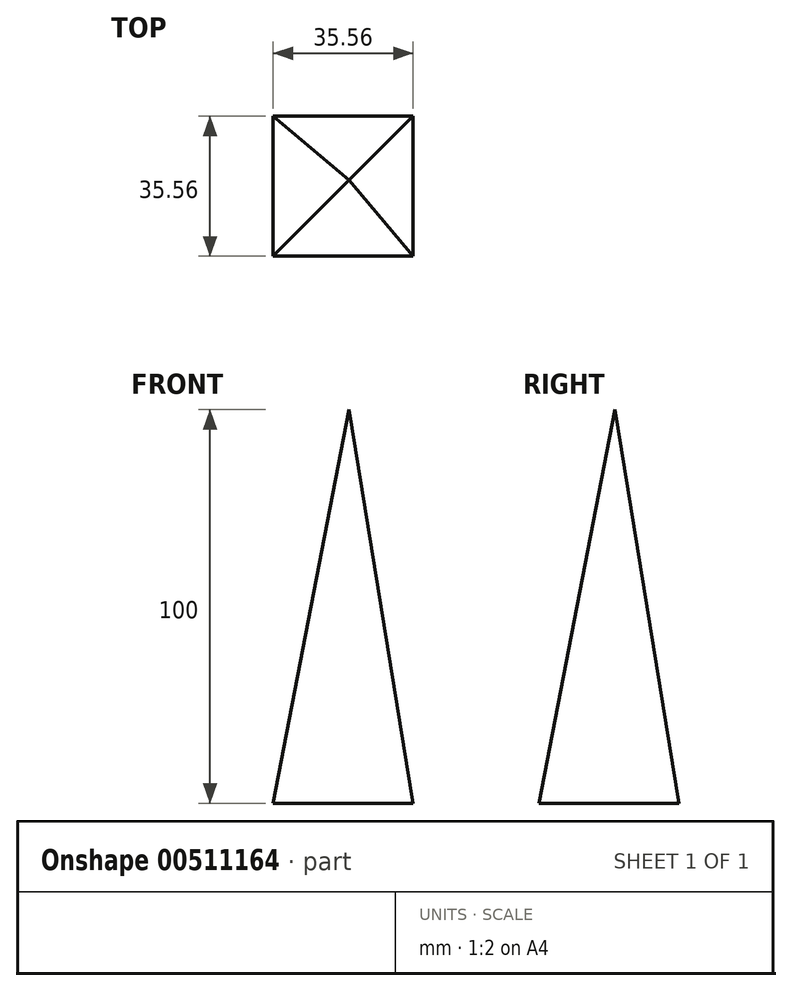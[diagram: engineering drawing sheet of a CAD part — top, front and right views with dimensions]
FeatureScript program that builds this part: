
annotation { "Feature Type Name" : "Feature", "Feature Type Description" : "" }
export const myFeature = defineFeature(function(context is Context, id is Id, definition is map)
    precondition{}
    {
        {
            var Q0;
            Q0=qCreatedBy(makeId("Top.planeOp"),FACE);
            var sketch = newSketch(context, id + "F0", { "sketchPlane" : qUnion([Q0])});
            skLineSegment(sketch, "E0", {"start": v(-19.24, 19.1) * mm, "end": v(-19.24, -16.47) * mm});
            skLineSegment(sketch, "E1", {"start": v(-19.24, -16.47) * mm, "end": v(16.32, -16.47) * mm});
            skLineSegment(sketch, "E2", {"start": v(16.32, -16.47) * mm, "end": v(16.32, 19.1) * mm});
            skLineSegment(sketch, "E3", {"start": v(17.2, 19.1) * mm, "end": v(-19.24, 19.1) * mm});
            skSolve(sketch);
        }
        {
            var Q0;
            Q0=qCreatedBy(makeId("Top.planeOp"),FACE);
            cPlane(context, id + "F1", {"entities" : qUnion([Q0]), "cplaneType" : CPlaneType.OFFSET, "offset" : 100 * mm, "width" : 152.4 * mm, "height" : 152.4 * mm});
        }
        {
            var Q0;
            Q0=qCreatedBy(id+"F1.planeOp",FACE);
            var sketch = newSketch(context, id + "F2", { "sketchPlane" : qUnion([Q0])});
            skPoint(sketch, "E4", {"position": v(0, 2.87) * mm});
            skSolve(sketch);
        }
        {
            var Q0;
            {var subQ0=sQuery(id+"F0.wireOp",EDGE,"E0");Q0=makeQuery(id+"F0.imprint","IMPRINT",FACE,{"disambiguationData":[TD([[makeQuery(id+"F0.imprint","IMPRINT",EDGE,{"derivedFrom":subQ0}),1.0]])]});}
            var Q1;
            Q1=sQuery(id+"F2.wireOp",VERTEX,"E4");
            loft(context, id + "F3", {"sheetProfilesArray" : [{ "sheetProfileEntities" : qUnion([Q0]) }, { "sheetProfileEntities" : qUnion([Q1]) }]});
        }
    });
